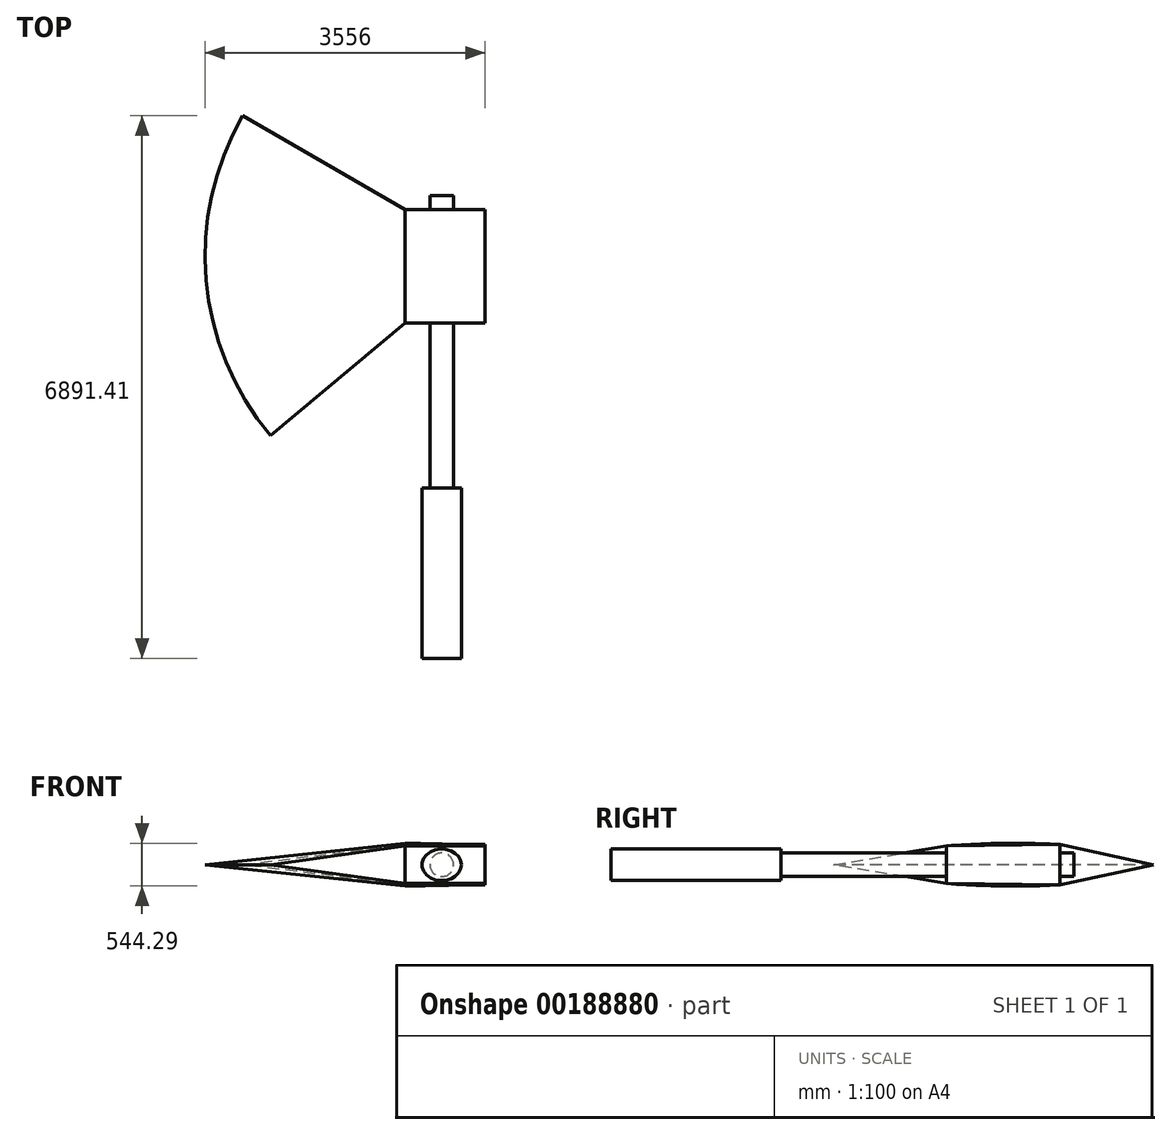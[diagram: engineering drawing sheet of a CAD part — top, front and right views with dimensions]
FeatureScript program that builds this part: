
annotation { "Feature Type Name" : "Feature", "Feature Type Description" : "" }
export const myFeature = defineFeature(function(context is Context, id is Id, definition is map)
    precondition{}
    {
        {
            var Q0;
            Q0=qCreatedBy(makeId("Front.planeOp"),FACE);
            var sketch = newSketch(context, id + "F0", { "sketchPlane" : qUnion([Q0])});
            skLineSegment(sketch, "E0", {"start": v(0, 383.43) * mm, "end": v(0, -378.57) * mm});
            skLineSegment(sketch, "E1", {"start": v(0, -378.57) * mm, "end": v(-3556, 0) * mm});
            skLineSegment(sketch, "E2", {"start": v(-3556, 0) * mm, "end": v(0, 383.43) * mm});
            skLineSegment(sketch, "E3", {"start": v(-3556, 0) * mm, "end": v(0, 0) * mm, "construction": true});
            skSolve(sketch);
        }
        {
            var Q0;
            Q0=makeQuery(id+"F0.imprint","IMPRINT",FACE,{"disambiguationData":[TD([[makeQuery(id+"F0.imprint","IMPRINT",EDGE,{"derivedFrom":sQuery(id+"F0.wireOp",EDGE,"E0")}),-1.0]])]});
            var Q1;
            Q1=sQuery(id+"F0.wireOp",EDGE,"E0");
            revolve(context, id + "F1", {"entities" : qUnion([Q0]), "axis" : qUnion([Q1]), "revolveType" : RevolveType.TWO_DIRECTIONS, "angle" : 30 * degree, "angleBack" : 320 * degree});
        }
        {
            var Q0;
            Q0=qCreatedBy(makeId("Top.planeOp"),FACE);
            var sketch = newSketch(context, id + "F2", { "sketchPlane" : qUnion([Q0])});
            skLineSegment(sketch, "E4", {"start": v(0, 0) * mm, "end": v(-1016, 586.59) * mm});
            skLineSegment(sketch, "E5", {"start": v(-1016, 586.59) * mm, "end": v(-1016, -852.53) * mm});
            skLineSegment(sketch, "E6", {"start": v(-1016, -852.53) * mm, "end": v(0, 0) * mm});
            skSolve(sketch);
        }
        {
            var Q0;
            Q0 = qSketchRegion(id + "F2", true);
            extrude(context, id + "F3", {"entities" : qUnion([Q0]), "operationType" : NewBodyOperationType.REMOVE, "endBound" : BoundingType.SYMMETRIC, "oppositeDirection" : true, "depth" : 1148.08 * mm});
        }
        {
            var Q0;
            Q0=qCreatedBy(makeId("Right.planeOp"),FACE);
            var sketch = newSketch(context, id + "F4", { "sketchPlane" : qUnion([Q0])});
            skLineSegment(sketch, "E7.0", {"start": v(-852.53, -237.37) * mm, "end": v(-852.53, 240.42) * mm});
            skLineSegment(sketch, "E8.0", {"start": v(586.59, -253.68) * mm, "end": v(586.59, 256.93) * mm});
            skLineSegment(sketch, "E9", {"start": v(-852.53, 240.42) * mm, "end": v(586.59, 256.93) * mm});
            skLineSegment(sketch, "E10", {"start": v(586.59, -253.68) * mm, "end": v(-852.53, -237.37) * mm});
            skSolve(sketch);
        }
        {
            var Q1;
            Q1=makeQuery(id+"F3.boolean.opBoolean","COPY",FACE,{"derivedFrom":makeQuery(id+"F3.opExtrude","SWEPT_FACE",FACE,{"disambiguationData":[OSD([sQuery(id+"F2.wireOp",EDGE,"E5")])]})});
            var Q2;
            Q2=makeQuery(id+"F4.imprint","IMPRINT",FACE,{"disambiguationData":[TD([[makeQuery(id+"F4.imprint","IMPRINT",EDGE,{"derivedFrom":sQuery(id+"F4.wireOp",EDGE,"E7.0")}),-1.0]])]});
            loft(context, id + "F5", {"operationType" : NewBodyOperationType.ADD, "sheetProfilesArray" : [{ "sheetProfileEntities" : qUnion([Q1]) }, { "sheetProfileEntities" : qUnion([Q2]) }]});
        }
        {
            var Q0;
            Q0=makeQuery(id+"F5.opLoft","SWEPT_FACE",FACE,{"disambiguationData":[OSD([sQuery(id+"F0.wireOp",EDGE,"E1"),sQuery(id+"F0.wireOp",EDGE,"E2"),sQuery(id+"F2.wireOp",EDGE,"E4"),sQuery(id+"F2.wireOp",EDGE,"E5"),sQuery(id+"F4.wireOp",EDGE,"E8.0"),sQuery(id+"F4.wireOp",EDGE,"E9"),sQuery(id+"F4.wireOp",EDGE,"E10")])]});
            var sketch = newSketch(context, id + "F6", { "sketchPlane" : qUnion([Q0])});
            skCircle(sketch, "E11", {"center": v(550, 0) * mm, "radius": 150 * mm});
            skLineSegment(sketch, "E12", {"start": v(0, 0) * mm, "end": v(1016, 0) * mm, "construction": true});
            skSolve(sketch);
        }
        {
            var Q0;
            Q0 = qSketchRegion(id + "F6", true);
            extrude(context, id + "F7", {"entities" : qUnion([Q0]), "operationType" : NewBodyOperationType.REMOVE, "endBound" : BoundingType.THROUGH_ALL, "oppositeDirection" : true, "depth" : 1920 * mm});
        }
        {
            var Q0;
            Q0=makeQuery(id+"F5.opLoft","SWEPT_FACE",FACE,{"disambiguationData":[OSD([sQuery(id+"F0.wireOp",EDGE,"E1"),sQuery(id+"F0.wireOp",EDGE,"E2"),sQuery(id+"F2.wireOp",EDGE,"E4"),sQuery(id+"F2.wireOp",EDGE,"E5"),sQuery(id+"F4.wireOp",EDGE,"E8.0"),sQuery(id+"F4.wireOp",EDGE,"E9"),sQuery(id+"F4.wireOp",EDGE,"E10")])]});
            var sketch = newSketch(context, id + "F8", { "sketchPlane" : qUnion([Q0])});
            skCircle(sketch, "E13.0", {"center": v(550, 0) * mm, "radius": 150 * mm});
            skSolve(sketch);
        }
        {
            var Q0;
            Q0=makeQuery(id+"F8.imprint","IMPRINT",FACE,{"disambiguationData":[TD([[makeQuery(id+"F8.imprint","IMPRINT",EDGE,{"derivedFrom":sQuery(id+"F8.wireOp",EDGE,"E13.0")}),1.0]])]});
            var Q1;
            Q1=makeQuery(id+"F5.opLoft","SWEPT_FACE",FACE,{"disambiguationData":[OSD([sQuery(id+"F0.wireOp",EDGE,"E1"),sQuery(id+"F0.wireOp",EDGE,"E2"),sQuery(id+"F2.wireOp",EDGE,"E4"),sQuery(id+"F2.wireOp",EDGE,"E5"),sQuery(id+"F4.wireOp",EDGE,"E8.0"),sQuery(id+"F4.wireOp",EDGE,"E9"),sQuery(id+"F4.wireOp",EDGE,"E10")])]});
            extrude(context, id + "F9", {"entities" : qUnion([Q0]), "operationType" : NewBodyOperationType.ADD, "endBoundEntityFace" : qUnion([Q1]), "depth" : 180 * mm, "hasSecondDirection" : true, "secondDirectionOppositeDirection" : true, "secondDirectionDepth" : 5700 * mm});
        }
        {
            var Q0;
            Q0=makeQuery(id+"F9.opExtrude","CAP_FACE",FACE,{"disambiguationData":[OSD([sQuery(id+"F8.wireOp",EDGE,"E13.0")])],"isStart":true});
            var sketch = newSketch(context, id + "F10", { "sketchPlane" : qUnion([Q0])});
            skEllipse(sketch, "E14", {"center": v(-550, 0) * mm, "majorRadius": 250 * mm, "minorRadius": 200 * mm, "majorAxis": v(1, 0)});
            skLineSegment(sketch, "E15", {"start": v(-800, 0) * mm, "end": v(-300, 0) * mm, "construction": true});
            skLineSegment(sketch, "E16", {"start": v(-550, 200) * mm, "end": v(-550, -200) * mm, "construction": true});
            skSolve(sketch);
        }
        {
            var Q0;
            Q0 = qSketchRegion(id + "F10", true);
            extrude(context, id + "F11", {"entities" : qUnion([Q0]), "operationType" : NewBodyOperationType.ADD, "oppositeDirection" : true, "depth" : 2160 * mm});
        }
    });
